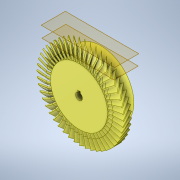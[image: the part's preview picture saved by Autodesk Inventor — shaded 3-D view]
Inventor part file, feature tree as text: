
AUTODESK INVENTOR PART (.ipt)
format: ipt  version: 2021.2 (Build 252289000, 289)  size: 3,072,512 bytes
history: native  units: in
note: dims shown in document units (in); Inventor stores cm internally (conversion verified against a paired STEP export)
features: extrude x5, sketch x5, plane x2, other x2, loft x1, pattern_circular x1
ambient origin geometry x8: Origin, YZ Plane, XZ Plane, XY Plane, X Axis, Y Axis, Z Axis, Center Point
bodies: Solid1 (feature_tree)
feature tree (16):
  extrude  "Extrusion1"  Depth=1.0in
  plane  "Work Plane1"
  sketch  "Sketch2"  dims[d3=1.5in d4=0.0312in]
  plane  "Work Plane2"
  sketch  "Sketch4"  dims[d13=2.0in d38=0.315in]
  extrude  "Extrusion3"  Depth=0.0312in
  sketch  "Sketch6"  dims[d41=0.0in d42=0.0in d43=3.9375in d47=0.0625in d49=0.3in d50=0.0in d51=0.2in d52=0.0in d53=0.0in d54=90.0deg d55=0.0in d56=90.0deg d57=18.8976in d58=360.0deg d60=0.0in d61=0.0in]
  extrude  "Extrusion5"  Depth=0.315in
  extrude  "Extrusion6"  Depth=0.125in
  loft  "Loft4"
  pattern_circular  "Circular Pattern7"  [2 undecoded]
  extrude  "Extrusion7"  Depth=0.3in TaperAngle=0.0deg
  sketch  "Sketch1"  dims[d0=2.6in d1=1.0in d2=0.0777in]
  sketch  "Sketch5"  dims[d39=0.125in d40=0.125in]
  other  "Edges4"
  other  "Edges5"
note: 2 required parameter values undecoded (feature->parameter linkage not recoverable at this tier; creation-order binding heuristic only, values carry confidence <= 0.55)
